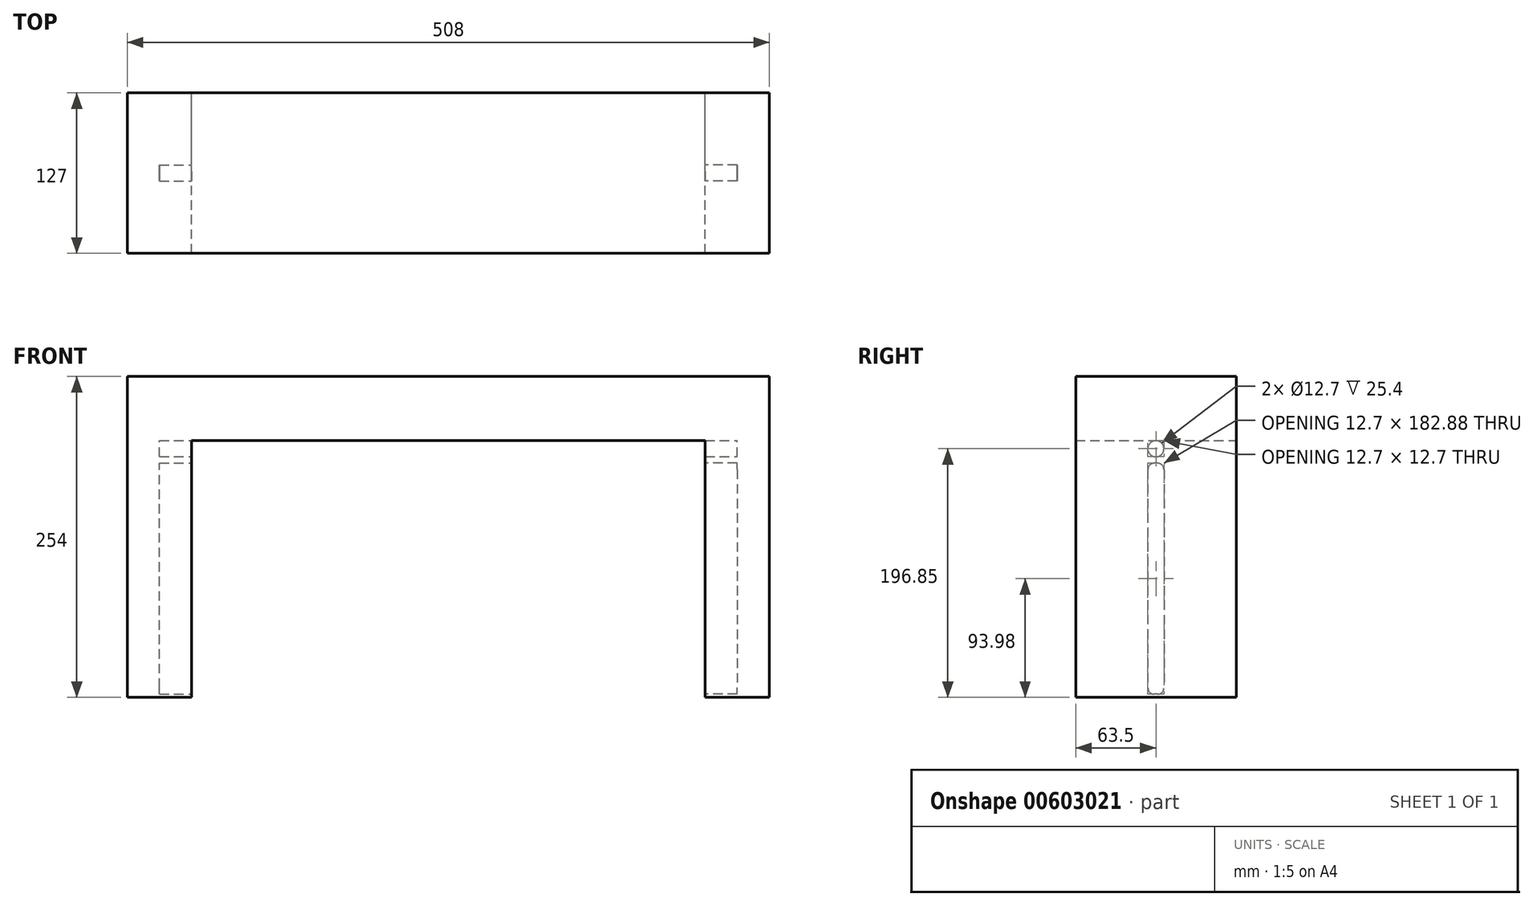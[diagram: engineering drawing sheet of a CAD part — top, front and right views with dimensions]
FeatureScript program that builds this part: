
annotation { "Feature Type Name" : "Feature", "Feature Type Description" : "" }
export const myFeature = defineFeature(function(context is Context, id is Id, definition is map)
    precondition{}
    {
        {
            var Q0;
            Q0=qCreatedBy(makeId("Front.planeOp"),FACE);
            var sketch = newSketch(context, id + "F0", { "sketchPlane" : qUnion([Q0])});
            skLineSegment(sketch, "E0.bottom", {"start": v(203.2, -101.6) * mm, "end": v(-203.2, -101.6) * mm});
            skLineSegment(sketch, "E0.top", {"start": v(203.2, 101.6) * mm, "end": v(-203.2, 101.6) * mm});
            skLineSegment(sketch, "E0.left", {"start": v(203.2, -101.6) * mm, "end": v(203.2, 101.6) * mm});
            skLineSegment(sketch, "E0.right", {"start": v(-203.2, -101.6) * mm, "end": v(-203.2, 101.6) * mm});
            skPoint(sketch, "E0.middle", {"position": v(0, 0) * mm});
            skLineSegment(sketch, "E1.bottom", {"start": v(254, -101.6) * mm, "end": v(-254, -101.6) * mm});
            skLineSegment(sketch, "E1.top", {"start": v(254, 101.6) * mm, "end": v(-254, 101.6) * mm});
            skLineSegment(sketch, "E1.left", {"start": v(254, -101.6) * mm, "end": v(254, 101.6) * mm});
            skLineSegment(sketch, "E1.right", {"start": v(-254, -101.6) * mm, "end": v(-254, 101.6) * mm});
            skLineSegment(sketch, "E2.bottom", {"start": v(-254, 101.6) * mm, "end": v(254, 101.6) * mm});
            skLineSegment(sketch, "E2.top", {"start": v(-254, 152.4) * mm, "end": v(254, 152.4) * mm});
            skLineSegment(sketch, "E2.left", {"start": v(-254, 101.6) * mm, "end": v(-254, 152.4) * mm});
            skLineSegment(sketch, "E2.right", {"start": v(254, 101.6) * mm, "end": v(254, 152.4) * mm});
            skSolve(sketch);
        }
        {
            var Q0;
            {var subQ0=sQuery(id+"F0.wireOp",EDGE,"E0.right");Q0=makeQuery(id+"F0.imprint","IMPRINT",FACE,{"disambiguationData":[TD([[makeQuery(id+"F0.imprint","IMPRINT",EDGE,{"derivedFrom":subQ0}),1.0]])]});}
            var Q1;
            {var subQ1=sQuery(id+"F0.wireOp",EDGE,"E0.top");Q1=makeQuery(id+"F0.imprint","IMPRINT",FACE,{"disambiguationData":[TD([[makeQuery(id+"F0.imprint","IMPRINT",EDGE,{"derivedFrom":subQ1}),-1.0]])]});}
            var Q2;
            {var subQ0=sQuery(id+"F0.wireOp",EDGE,"E0.left");Q2=makeQuery(id+"F0.imprint","IMPRINT",FACE,{"disambiguationData":[TD([[makeQuery(id+"F0.imprint","IMPRINT",EDGE,{"derivedFrom":subQ0}),-1.0]])]});}
            extrude(context, id + "F1", {"entities" : qUnion([Q0, Q1, Q2]), "endBound" : BoundingType.SYMMETRIC, "depth" : 127 * mm, "offsetDistance" : 25.4 * mm});
        }
        {
            var Q0;
            Q0=qCreatedBy(makeId("Front.planeOp"),FACE);
            var sketch = newSketch(context, id + "F2", { "sketchPlane" : qUnion([Q0])});
            skLineSegment(sketch, "E3", {"start": v(0, 0) * mm, "end": v(203.2, 0) * mm});
            skLineSegment(sketch, "E4", {"start": v(203.2, 0) * mm, "end": v(203.2, 101.6) * mm});
            skLineSegment(sketch, "E5", {"start": v(0, 0) * mm, "end": v(0, 25.4) * mm});
            skLineSegment(sketch, "E6", {"start": v(203.2, 101.6) * mm, "end": v(228.6, 101.6) * mm});
            skLineSegment(sketch, "E7", {"start": v(228.6, 101.6) * mm, "end": v(228.6, 95.25) * mm});
            skLineSegment(sketch, "E8", {"start": v(228.6, 95.25) * mm, "end": v(203.2, 95.25) * mm});
            skLineSegment(sketch, "E9.MirrorCS", {"start": v(0, 0) * mm, "end": v(-203.2, 0) * mm});
            skLineSegment(sketch, "E10.MirrorCS", {"start": v(-203.2, 0) * mm, "end": v(-203.2, 101.6) * mm});
            skLineSegment(sketch, "E11.MirrorCS", {"start": v(-203.2, 101.6) * mm, "end": v(-228.6, 101.6) * mm});
            skLineSegment(sketch, "E12.MirrorCS", {"start": v(-228.6, 95.25) * mm, "end": v(-203.2, 95.25) * mm});
            skLineSegment(sketch, "E13.MirrorCS", {"start": v(-228.6, 101.6) * mm, "end": v(-228.6, 95.25) * mm});
            skSolve(sketch);
        }
        {
            var Q0;
            Q0 = qSketchRegion(id + "F2", true);
            var Q1;
            Q1=sQuery(id+"F2.wireOp",EDGE,"E12.MirrorCS");
            revolve(context, id + "F3", {"operationType" : NewBodyOperationType.REMOVE, "entities" : qUnion([Q0]), "axis" : qUnion([Q1]), "revolveType" : RevolveType.FULL, "oppositeDirection" : true});
        }
        {
            var Q0;
            Q0=qCreatedBy(makeId("Front.planeOp"),FACE);
            var sketch = newSketch(context, id + "F4", { "sketchPlane" : qUnion([Q0])});
            skLineSegment(sketch, "E14", {"start": v(0, 0) * mm, "end": v(203.2, 0) * mm});
            skLineSegment(sketch, "E15", {"start": v(203.2, 0) * mm, "end": v(203.2, -101.6) * mm});
            skLineSegment(sketch, "E16", {"start": v(228.6, -92.71) * mm, "end": v(228.6, -99.06) * mm});
            skLineSegment(sketch, "E17", {"start": v(228.6, -99.06) * mm, "end": v(203.2, -99.06) * mm});
            skLineSegment(sketch, "E18", {"start": v(228.6, -99.06) * mm, "end": v(228.6, 83.82) * mm});
            skPoint(sketch, "E18.endSnap0", {"position": v(228.6, -95.89) * mm});
            skLineSegment(sketch, "E19", {"start": v(228.6, 83.82) * mm, "end": v(203.2, 83.82) * mm});
            skLineSegment(sketch, "E20", {"start": v(203.2, 83.82) * mm, "end": v(203.2, 0) * mm});
            skLineSegment(sketch, "E21", {"start": v(0, 0) * mm, "end": v(0, 25.4) * mm});
            skLineSegment(sketch, "E22.MirrorCS", {"start": v(0, 0) * mm, "end": v(-203.2, 0) * mm});
            skLineSegment(sketch, "E23.MirrorCS", {"start": v(-203.2, 83.82) * mm, "end": v(-203.2, 0) * mm});
            skLineSegment(sketch, "E24.MirrorCS", {"start": v(-228.6, -99.06) * mm, "end": v(-228.6, 83.82) * mm});
            skLineSegment(sketch, "E25.MirrorCS", {"start": v(-228.6, 83.82) * mm, "end": v(-203.2, 83.82) * mm});
            skLineSegment(sketch, "E26.MirrorCS", {"start": v(-228.6, -99.06) * mm, "end": v(-203.2, -99.06) * mm});
            skLineSegment(sketch, "E27.MirrorCS", {"start": v(-203.2, 0) * mm, "end": v(-203.2, -101.6) * mm});
            skSolve(sketch);
        }
        {
            var Q0;
            Q0 = qSketchRegion(id + "F4", true);
            extrude(context, id + "F5", {"entities" : qUnion([Q0]), "operationType" : NewBodyOperationType.REMOVE, "endBound" : BoundingType.SYMMETRIC, "oppositeDirection" : true, "depth" : 12.7 * mm, "offsetDistance" : 25.4 * mm});
        }
        {
            var Q0;
            Q0=makeQuery(id+"F5.boolean.opBoolean","COPY",EDGE,{"derivedFrom":makeQuery(id+"F5.opExtrude","CAP_EDGE",EDGE,{"disambiguationData":[OSD([sQuery(id+"F4.wireOp",EDGE,"E25.MirrorCS")])],"isStart":false})});
            var Q1;
            Q1=makeQuery(id+"F5.boolean.opBoolean","COPY",EDGE,{"derivedFrom":makeQuery(id+"F5.opExtrude","CAP_EDGE",EDGE,{"disambiguationData":[OSD([sQuery(id+"F4.wireOp",EDGE,"E25.MirrorCS")])],"isStart":true})});
            var Q2;
            Q2=makeQuery(id+"F5.boolean.opBoolean","COPY",EDGE,{"derivedFrom":makeQuery(id+"F5.opExtrude","CAP_EDGE",EDGE,{"disambiguationData":[OSD([sQuery(id+"F4.wireOp",EDGE,"E26.MirrorCS")])],"isStart":true})});
            var Q3;
            Q3=makeQuery(id+"F5.boolean.opBoolean","COPY",EDGE,{"derivedFrom":makeQuery(id+"F5.opExtrude","CAP_EDGE",EDGE,{"disambiguationData":[OSD([sQuery(id+"F4.wireOp",EDGE,"E26.MirrorCS")])],"isStart":false})});
            var Q4;
            Q4=makeQuery(id+"F5.boolean.opBoolean","COPY",EDGE,{"derivedFrom":makeQuery(id+"F5.opExtrude","CAP_EDGE",EDGE,{"disambiguationData":[OSD([sQuery(id+"F4.wireOp",EDGE,"E19")])],"isStart":false})});
            var Q5;
            Q5=makeQuery(id+"F5.boolean.opBoolean","COPY",EDGE,{"derivedFrom":makeQuery(id+"F5.opExtrude","CAP_EDGE",EDGE,{"disambiguationData":[OSD([sQuery(id+"F4.wireOp",EDGE,"E19")])],"isStart":true})});
            var Q6;
            Q6=makeQuery(id+"F5.boolean.opBoolean","COPY",EDGE,{"derivedFrom":makeQuery(id+"F5.opExtrude","CAP_EDGE",EDGE,{"disambiguationData":[OSD([sQuery(id+"F4.wireOp",EDGE,"E17")])],"isStart":false})});
            var Q7;
            Q7=makeQuery(id+"F5.boolean.opBoolean","COPY",EDGE,{"derivedFrom":makeQuery(id+"F5.opExtrude","CAP_EDGE",EDGE,{"disambiguationData":[OSD([sQuery(id+"F4.wireOp",EDGE,"E17")])],"isStart":true})});
            fillet(context, id + "F6", {"entities" : qUnion([Q0, Q1, Q2, Q3, Q4, Q5, Q6, Q7]), "radius" : 5.08 * mm, "tangentPropagation" : true, "allowEdgeOverflow" : false});
        }
    });
